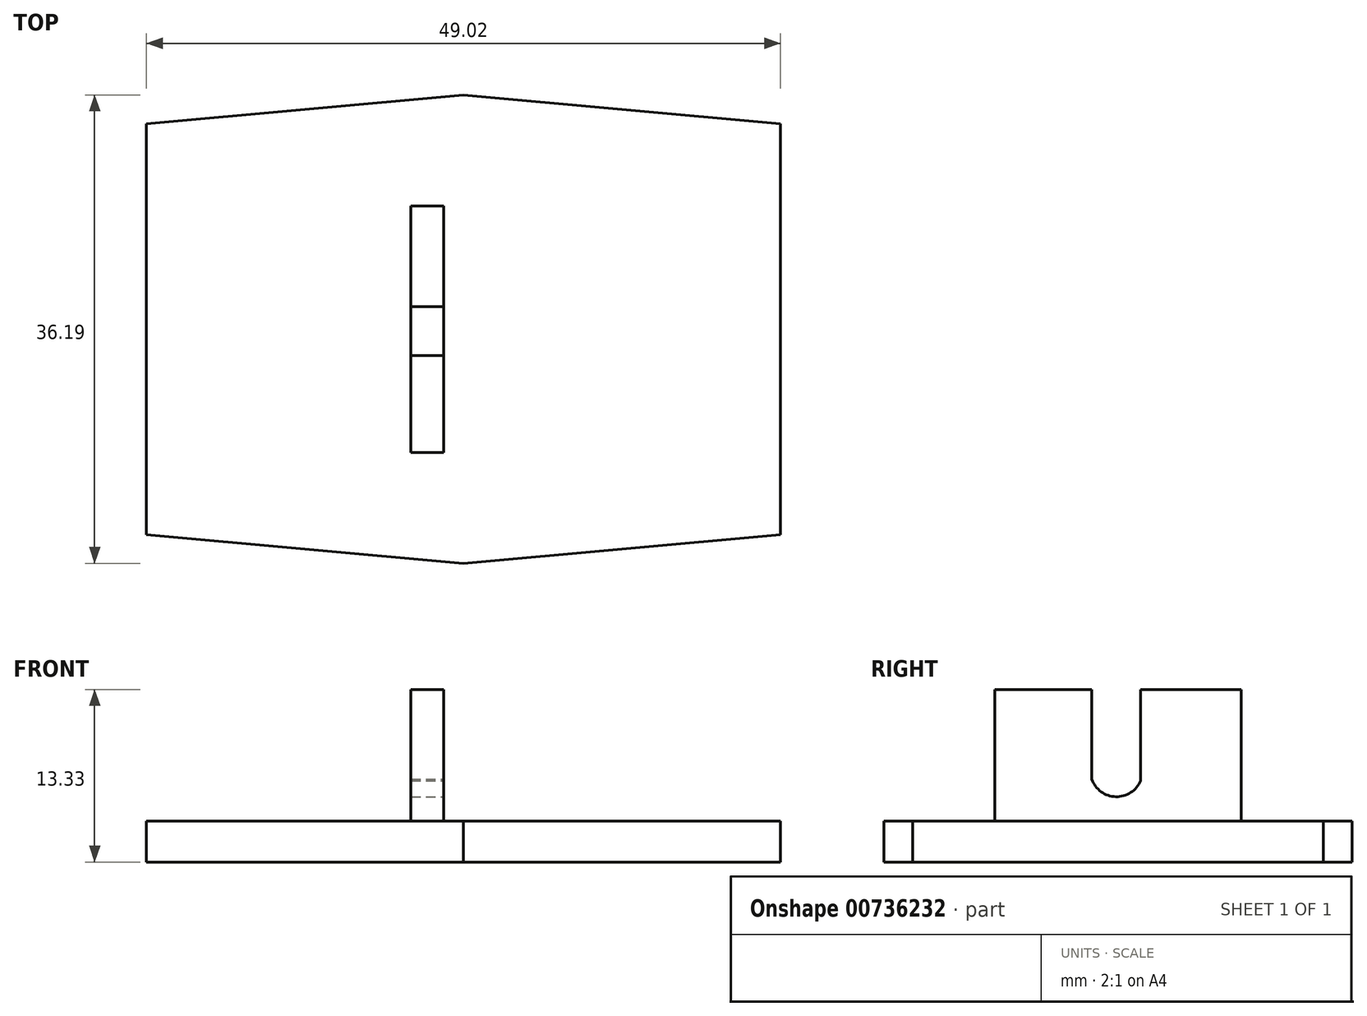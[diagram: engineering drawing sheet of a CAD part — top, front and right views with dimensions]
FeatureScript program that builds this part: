
annotation { "Feature Type Name" : "Feature", "Feature Type Description" : "" }
export const myFeature = defineFeature(function(context is Context, id is Id, definition is map)
    precondition{}
    {
        {
            var Q0;
            Q0=qCreatedBy(makeId("Top.planeOp"),FACE);
            var sketch = newSketch(context, id + "F0", { "sketchPlane" : qUnion([Q0])});
            skLineSegment(sketch, "E0.left", {"start": v(0, 0) * mm, "end": v(0, 31.75) * mm});
            skLineSegment(sketch, "E0.right", {"start": v(49.02, 0) * mm, "end": v(49.02, 31.75) * mm});
            skPoint(sketch, "E1.endSnap0", {"position": v(30.33, -8.47) * mm});
            skLineSegment(sketch, "E2", {"start": v(0, 31.75) * mm, "end": v(24.51, 33.97) * mm});
            skLineSegment(sketch, "E3", {"start": v(49.02, 31.75) * mm, "end": v(24.51, 33.97) * mm});
            skLineSegment(sketch, "E4", {"start": v(24.51, -2.22) * mm, "end": v(0, 0) * mm});
            skLineSegment(sketch, "E5", {"start": v(24.51, -2.22) * mm, "end": v(49.02, 0) * mm});
            skSolve(sketch);
        }
        {
            var Q0;
            Q0=makeQuery(id+"F0.imprint","IMPRINT",FACE,{"disambiguationData":[TD([[makeQuery(id+"F0.imprint","IMPRINT",EDGE,{"derivedFrom":sQuery(id+"F0.wireOp",EDGE,"E0.left")}),-1.0]])]});
            extrude(context, id + "F1", {"entities" : qUnion([Q0]), "depth" : 3.17 * mm, "offsetDistance" : 25.4 * mm});
        }
        {
            var Q0;
            Q0=makeQuery(id+"F1.opExtrude","CAP_FACE",FACE,{"disambiguationData":[OSD([sQuery(id+"F0.wireOp",EDGE,"E0.left"),sQuery(id+"F0.wireOp",EDGE,"E0.right"),sQuery(id+"F0.wireOp",EDGE,"E2"),sQuery(id+"F0.wireOp",EDGE,"E3"),sQuery(id+"F0.wireOp",EDGE,"E4"),sQuery(id+"F0.wireOp",EDGE,"E5")])],"isStart":false});
            var sketch = newSketch(context, id + "F2", { "sketchPlane" : qUnion([Q0])});
            skLineSegment(sketch, "E6.bottom", {"start": v(20.45, 25.4) * mm, "end": v(22.99, 25.4) * mm});
            skLineSegment(sketch, "E6.top", {"start": v(20.45, 6.35) * mm, "end": v(22.99, 6.35) * mm});
            skLineSegment(sketch, "E6.left", {"start": v(20.45, 25.4) * mm, "end": v(20.45, 6.35) * mm});
            skLineSegment(sketch, "E6.right", {"start": v(22.99, 25.4) * mm, "end": v(22.99, 6.35) * mm});
            skSolve(sketch);
        }
        {
            var Q0;
            Q0 = qSketchRegion(id + "F2", true);
            extrude(context, id + "F3", {"entities" : qUnion([Q0]), "operationType" : NewBodyOperationType.ADD, "depth" : 10.16 * mm, "offsetDistance" : 25.4 * mm});
        }
        {
            var Q0;
            Q0=makeQuery(id+"F3.opExtrude","SWEPT_FACE",FACE,{"disambiguationData":[OSD([sQuery(id+"F2.wireOp",EDGE,"E6.right")])]});
            var sketch = newSketch(context, id + "F4", { "sketchPlane" : qUnion([Q0])});
            skLineSegment(sketch, "E7.0", {"start": v(17.63, 13.33) * mm, "end": v(17.63, 6.29) * mm});
            skLineSegment(sketch, "E8.0", {"start": v(13.84, 13.34) * mm, "end": v(13.84, 6.39) * mm});
            skArc(sketch, "E9", {"start": v(13.84, 6.39) * mm, "mid": v(15.7, 5.05) * mm, "end": v(17.63, 6.29) * mm});
            skLineSegment(sketch, "E10", {"start": v(13.84, 13.34) * mm, "end": v(17.63, 13.33) * mm});
            skSolve(sketch);
        }
        {
            var Q0;
            Q0 = qSketchRegion(id + "F4", true);
            extrude(context, id + "F5", {"entities" : qUnion([Q0]), "operationType" : NewBodyOperationType.REMOVE, "oppositeDirection" : true, "depth" : 5.08 * mm, "offsetDistance" : 25.4 * mm});
        }
    });
